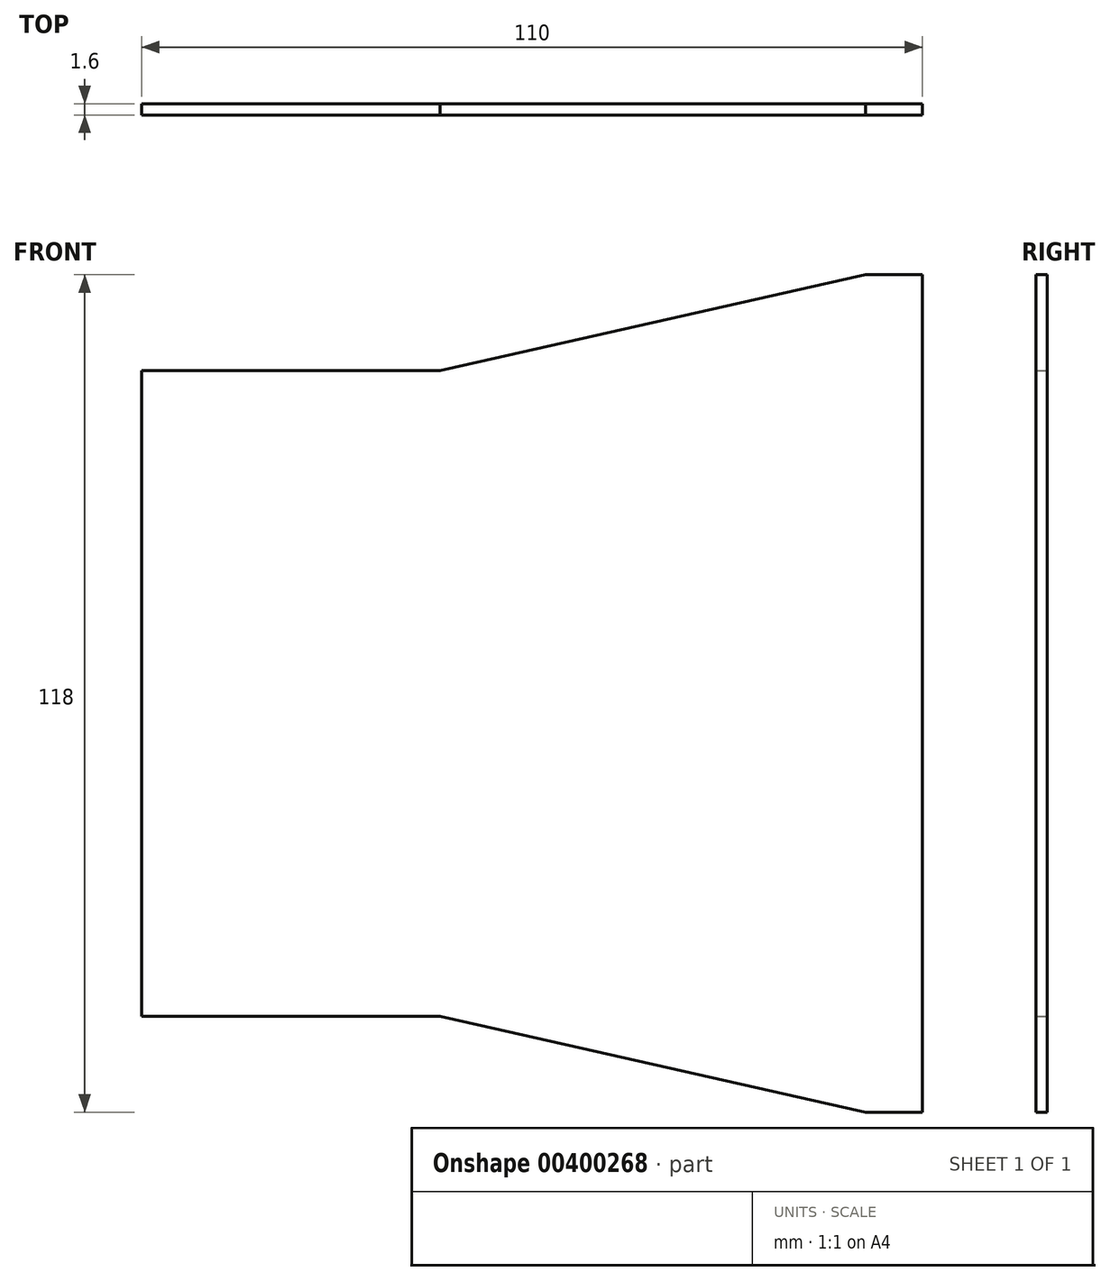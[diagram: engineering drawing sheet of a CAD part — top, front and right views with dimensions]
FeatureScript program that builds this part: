
annotation { "Feature Type Name" : "Feature", "Feature Type Description" : "" }
export const myFeature = defineFeature(function(context is Context, id is Id, definition is map)
    precondition{}
    {
        {
            var Q0;
            Q0=qCreatedBy(makeId("Front.planeOp"),FACE);
            var sketch = newSketch(context, id + "F0", { "sketchPlane" : qUnion([Q0])});
            skLineSegment(sketch, "E0", {"start": v(-7.14, 118) * mm, "end": v(-67.05, 104.5) * mm});
            skLineSegment(sketch, "E1", {"start": v(-67.05, 104.5) * mm, "end": v(-109.14, 104.5) * mm});
            skLineSegment(sketch, "E2", {"start": v(-109.14, 104.5) * mm, "end": v(-109.14, 13.5) * mm});
            skLineSegment(sketch, "E3", {"start": v(-109.14, 13.5) * mm, "end": v(-67.05, 13.5) * mm});
            skLineSegment(sketch, "E4", {"start": v(0.86, 0) * mm, "end": v(0.86, 118) * mm});
            skLineSegment(sketch, "E5", {"start": v(0.86, 118) * mm, "end": v(-7.14, 118) * mm});
            skLineSegment(sketch, "E6", {"start": v(0.86, 59) * mm, "end": v(-109.14, 59) * mm, "construction": true});
            skLineSegment(sketch, "E7", {"start": v(0.86, 0) * mm, "end": v(-7.14, 0) * mm});
            skLineSegment(sketch, "E8", {"start": v(-67.05, 13.5) * mm, "end": v(-7.14, 0) * mm});
            skSolve(sketch);
        }
        {
            var Q0;
            Q0=makeQuery(id+"F0.imprint","IMPRINT",FACE,{"disambiguationData":[TD([[makeQuery(id+"F0.imprint","IMPRINT",EDGE,{"derivedFrom":sQuery(id+"F0.wireOp",EDGE,"E0")}),1.0]])]});
            extrude(context, id + "F1", {"entities" : qUnion([Q0]), "depth" : 1.6 * mm, "offsetDistance" : 25 * mm});
        }
    });
